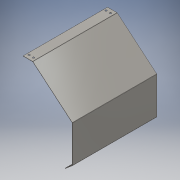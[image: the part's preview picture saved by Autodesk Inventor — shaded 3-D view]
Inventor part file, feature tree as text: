
AUTODESK INVENTOR PART (.ipt)
format: ipt  version: 2016 (Build 200138000, 138)  size: 218,112 bytes
history: native  units: mm
features: sheet_metal_op x10, sketch x6, other x5, hole x2
ambient origin geometry x8: Origin, YZ Plane, XZ Plane, XY Plane, X Axis, Y Axis, Z Axis, Center Point
bodies: Solid1 (feature_tree)
feature tree (23):
  sheet_metal_op  "Face1"
  sheet_metal_op  "Flange1"
  sheet_metal_op  "Flange2"
  sheet_metal_op  "Flange3"
  hole  "Hole1"  [1 undecoded]
  hole  "Hole2"  [1 undecoded]
  sketch  "Sketch1"  dims[d0=570.0mm d1=251.0mm]
  other  "Plate1"
  sketch  "Sketch2"  dims[d2=1.6mm d3=1.6mm]
  other  "Plate2"
  sheet_metal_op  "Bend1"
  sheet_metal_op  "Corner1"
  sketch  "Sketch3"  dims[d4=0.8mm]
  other  "Plate3"
  sheet_metal_op  "Bend2"
  sheet_metal_op  "Corner2"
  sketch  "Sketch4"  dims[d5=3.2mm]
  other  "Plate4"
  sheet_metal_op  "Bend3"
  sheet_metal_op  "Corner3"
  sketch  "Sketch5"  dims[d6=1.6mm]
  sketch  "Sketch6"  dims[d7=350.0mm d8=-8.726646mm d9=1.6mm d10=6.4mm d11=1.6mm d12=1.6mm d13=1.6mm d14=0.8mm d15=3.2mm d16=1.6mm d17=65.0mm d18=-6.981317mm d19=1.6mm d20=6.4mm d21=1.6mm d22=1.6mm d23=1.6mm d24=0.8mm d25=3.2mm d26=1.6mm d27=65.0mm d28=-8.726646mm d29=1.6mm d30=6.4mm d31=1.6mm d32=1.6mm d33=60.0mm d34=12.0mm d35=12.0mm d36=15.0mm d37=15.0mm d38=25.0mm d39=25.0mm d40=12.0mm d41=12.0mm d42=25.0mm d43=25.0mm d44=12.0mm d45=6.0mm d46=4.0mm d47=2.0mm d48=90.0deg d49=1.6mm d50=20.594885mm d51=60.0mm d52=12.0mm d53=12.0mm d54=25.0mm d55=25.0mm d56=15.0mm d57=15.0mm d58=12.0mm d59=12.0mm d60=25.0mm d61=25.0mm d62=12.0mm d63=6.0mm d64=4.0mm d65=2.0mm d66=90.0deg d67=1.6mm d68=20.594885mm]
  other  "Definition1"
note: 2 required parameter values undecoded (feature->parameter linkage not recoverable at this tier; creation-order binding heuristic only, values carry confidence <= 0.55)
